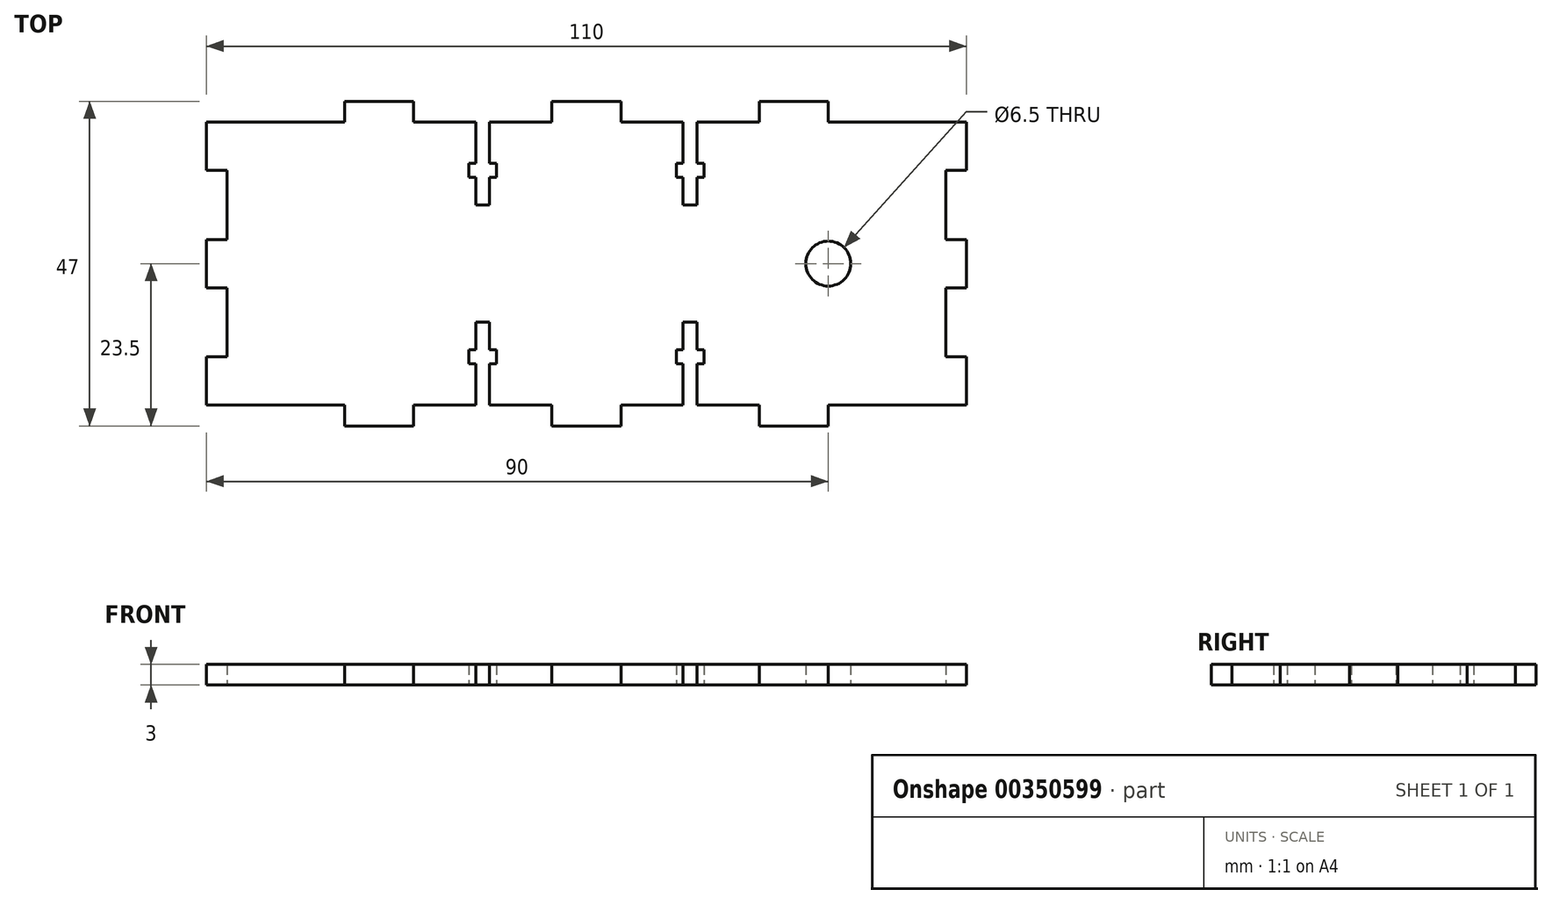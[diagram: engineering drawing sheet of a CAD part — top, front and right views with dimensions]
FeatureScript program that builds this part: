
annotation { "Feature Type Name" : "Feature", "Feature Type Description" : "" }
export const myFeature = defineFeature(function(context is Context, id is Id, definition is map)
    precondition{}
    {
        {
            var Q0;
            Q0=qCreatedBy(makeId("Top.planeOp"),FACE);
            var sketch = newSketch(context, id + "F0", { "sketchPlane" : qUnion([Q0])});
            skLineSegment(sketch, "E0", {"start": v(-110, 44) * mm, "end": v(-90, 44) * mm});
            skLineSegment(sketch, "E1", {"start": v(-90, 44) * mm, "end": v(-90, 47) * mm});
            skLineSegment(sketch, "E2", {"start": v(-90, 47) * mm, "end": v(-80, 47) * mm});
            skLineSegment(sketch, "E3", {"start": v(-80, 47) * mm, "end": v(-80, 44) * mm});
            skLineSegment(sketch, "E4", {"start": v(-60, 44) * mm, "end": v(-60, 47) * mm});
            skLineSegment(sketch, "E5", {"start": v(-60, 0) * mm, "end": v(-60, 3) * mm});
            skLineSegment(sketch, "E6", {"start": v(-80, 3) * mm, "end": v(-80, 0) * mm});
            skLineSegment(sketch, "E7", {"start": v(-80, 0) * mm, "end": v(-90, 0) * mm});
            skLineSegment(sketch, "E8", {"start": v(-90, 0) * mm, "end": v(-90, 3) * mm});
            skLineSegment(sketch, "E9", {"start": v(-90, 3) * mm, "end": v(-110, 3) * mm});
            skLineSegment(sketch, "E10", {"start": v(-110, 44) * mm, "end": v(-110, 37) * mm});
            skLineSegment(sketch, "E11", {"start": v(-110, 37) * mm, "end": v(-107, 37) * mm});
            skLineSegment(sketch, "E12", {"start": v(-107, 37) * mm, "end": v(-107, 27) * mm});
            skLineSegment(sketch, "E13", {"start": v(-107, 27) * mm, "end": v(-110, 27) * mm});
            skLineSegment(sketch, "E14", {"start": v(-110, 27) * mm, "end": v(-110, 20) * mm});
            skLineSegment(sketch, "E15", {"start": v(-110, 20) * mm, "end": v(-107, 20) * mm});
            skLineSegment(sketch, "E16", {"start": v(-107, 20) * mm, "end": v(-107, 10) * mm});
            skLineSegment(sketch, "E17", {"start": v(-107, 10) * mm, "end": v(-110, 10) * mm});
            skLineSegment(sketch, "E18", {"start": v(-110, 10) * mm, "end": v(-110, 3) * mm});
            skLineSegment(sketch, "E19", {"start": v(-80, 3) * mm, "end": v(-71, 3) * mm});
            skLineSegment(sketch, "E20", {"start": v(-71, 3) * mm, "end": v(-71, 9) * mm});
            skLineSegment(sketch, "E21", {"start": v(-71, 9) * mm, "end": v(-72, 9) * mm});
            skLineSegment(sketch, "E22", {"start": v(-72, 9) * mm, "end": v(-72, 11) * mm});
            skLineSegment(sketch, "E23", {"start": v(-72, 11) * mm, "end": v(-71, 11) * mm});
            skLineSegment(sketch, "E24", {"start": v(-71, 11) * mm, "end": v(-71, 15) * mm});
            skLineSegment(sketch, "E25", {"start": v(-71, 15) * mm, "end": v(-69, 15) * mm});
            skLineSegment(sketch, "E26", {"start": v(-69, 15) * mm, "end": v(-69, 11) * mm});
            skLineSegment(sketch, "E27", {"start": v(-69, 11) * mm, "end": v(-68, 11) * mm});
            skLineSegment(sketch, "E28", {"start": v(-68, 11) * mm, "end": v(-68, 9) * mm});
            skLineSegment(sketch, "E29", {"start": v(-68, 9) * mm, "end": v(-69, 9) * mm});
            skLineSegment(sketch, "E30", {"start": v(-69, 9) * mm, "end": v(-69, 3) * mm});
            skLineSegment(sketch, "E31", {"start": v(-80, 44) * mm, "end": v(-71, 44) * mm});
            skLineSegment(sketch, "E32", {"start": v(-60, 44) * mm, "end": v(-69, 44) * mm});
            skLineSegment(sketch, "E33", {"start": v(-69, 44) * mm, "end": v(-69, 38) * mm});
            skLineSegment(sketch, "E34", {"start": v(-69, 38) * mm, "end": v(-68, 38) * mm});
            skLineSegment(sketch, "E35", {"start": v(-68, 38) * mm, "end": v(-68, 36) * mm});
            skLineSegment(sketch, "E36", {"start": v(-68, 36) * mm, "end": v(-69, 36) * mm});
            skLineSegment(sketch, "E37", {"start": v(-69, 36) * mm, "end": v(-69, 32) * mm});
            skLineSegment(sketch, "E38", {"start": v(-69, 32) * mm, "end": v(-71, 32) * mm});
            skLineSegment(sketch, "E39", {"start": v(-71, 32) * mm, "end": v(-71, 36) * mm});
            skLineSegment(sketch, "E40", {"start": v(-71, 36) * mm, "end": v(-72, 36) * mm});
            skLineSegment(sketch, "E41", {"start": v(-72, 36) * mm, "end": v(-72, 38) * mm});
            skLineSegment(sketch, "E42", {"start": v(-72, 38) * mm, "end": v(-71, 38) * mm});
            skLineSegment(sketch, "E43", {"start": v(-71, 38) * mm, "end": v(-71, 44) * mm});
            skLineSegment(sketch, "E44", {"start": v(-69, 3) * mm, "end": v(-60, 3) * mm});
            skLineSegment(sketch, "E45", {"start": v(-60, 47) * mm, "end": v(-55, 47) * mm});
            skLineSegment(sketch, "E46", {"start": v(-60, 0) * mm, "end": v(-55, 0) * mm});
            skLineSegment(sketch, "E47.MirrorCS", {"start": v(-42, 38) * mm, "end": v(-42, 36) * mm});
            skLineSegment(sketch, "E48.MirrorCS", {"start": v(-41, 38) * mm, "end": v(-42, 38) * mm});
            skLineSegment(sketch, "E49.MirrorCS", {"start": v(-42, 9) * mm, "end": v(-41, 9) * mm});
            skLineSegment(sketch, "E50.MirrorCS", {"start": v(-42, 36) * mm, "end": v(-41, 36) * mm});
            skLineSegment(sketch, "E51.MirrorCS", {"start": v(-39, 32) * mm, "end": v(-39, 36) * mm});
            skLineSegment(sketch, "E52.MirrorCS", {"start": v(-41, 32) * mm, "end": v(-39, 32) * mm});
            skLineSegment(sketch, "E53.MirrorCS", {"start": v(-42, 11) * mm, "end": v(-42, 9) * mm});
            skLineSegment(sketch, "E54.MirrorCS", {"start": v(-39, 36) * mm, "end": v(-38, 36) * mm});
            skLineSegment(sketch, "E55.MirrorCS", {"start": v(-38, 9) * mm, "end": v(-38, 11) * mm});
            skLineSegment(sketch, "E56.MirrorCS", {"start": v(-39, 15) * mm, "end": v(-41, 15) * mm});
            skLineSegment(sketch, "E57.MirrorCS", {"start": v(-39, 9) * mm, "end": v(-38, 9) * mm});
            skLineSegment(sketch, "E58.MirrorCS", {"start": v(-38, 11) * mm, "end": v(-39, 11) * mm});
            skLineSegment(sketch, "E59.MirrorCS", {"start": v(0, 37) * mm, "end": v(-3, 37) * mm});
            skLineSegment(sketch, "E60.MirrorCS", {"start": v(-50, 0) * mm, "end": v(-50, 3) * mm});
            skLineSegment(sketch, "E61.MirrorCS", {"start": v(-30, 3) * mm, "end": v(-30, 0) * mm});
            skLineSegment(sketch, "E62.MirrorCS", {"start": v(-50, 44) * mm, "end": v(-50, 47) * mm});
            skLineSegment(sketch, "E63.MirrorCS", {"start": v(-38, 36) * mm, "end": v(-38, 38) * mm});
            skLineSegment(sketch, "E64.MirrorCS", {"start": v(-3, 10) * mm, "end": v(0, 10) * mm});
            skLineSegment(sketch, "E65.MirrorCS", {"start": v(-41, 11) * mm, "end": v(-42, 11) * mm});
            skLineSegment(sketch, "E66.MirrorCS", {"start": v(-41, 15) * mm, "end": v(-41, 11) * mm});
            skLineSegment(sketch, "E67.MirrorCS", {"start": v(-38, 38) * mm, "end": v(-39, 38) * mm});
            skLineSegment(sketch, "E68.MirrorCS", {"start": v(-20, 0) * mm, "end": v(-20, 3) * mm});
            skLineSegment(sketch, "E69.MirrorCS", {"start": v(-3, 27) * mm, "end": v(0, 27) * mm});
            skLineSegment(sketch, "E70.MirrorCS", {"start": v(-39, 11) * mm, "end": v(-39, 15) * mm});
            skLineSegment(sketch, "E71.MirrorCS", {"start": v(-41, 36) * mm, "end": v(-41, 32) * mm});
            skLineSegment(sketch, "E72.MirrorCS", {"start": v(-20, 44) * mm, "end": v(-20, 47) * mm});
            skLineSegment(sketch, "E73.MirrorCS", {"start": v(-30, 47) * mm, "end": v(-30, 44) * mm});
            skLineSegment(sketch, "E74.MirrorCS", {"start": v(0, 20) * mm, "end": v(-3, 20) * mm});
            skLineSegment(sketch, "E75.MirrorCS", {"start": v(-39, 3) * mm, "end": v(-39, 9) * mm});
            skLineSegment(sketch, "E76.MirrorCS", {"start": v(-41, 44) * mm, "end": v(-41, 38) * mm});
            skLineSegment(sketch, "E77.MirrorCS", {"start": v(0, 10) * mm, "end": v(0, 3) * mm});
            skLineSegment(sketch, "E78.MirrorCS", {"start": v(-20, 3) * mm, "end": v(0, 3) * mm});
            skLineSegment(sketch, "E79.MirrorCS", {"start": v(-3, 37) * mm, "end": v(-3, 27) * mm});
            skLineSegment(sketch, "E80.MirrorCS", {"start": v(-39, 38) * mm, "end": v(-39, 44) * mm});
            skLineSegment(sketch, "E81.MirrorCS", {"start": v(0, 27) * mm, "end": v(0, 20) * mm});
            skLineSegment(sketch, "E82.MirrorCS", {"start": v(0, 44) * mm, "end": v(-20, 44) * mm});
            skLineSegment(sketch, "E83.MirrorCS", {"start": v(-3, 20) * mm, "end": v(-3, 10) * mm});
            skLineSegment(sketch, "E84.MirrorCS", {"start": v(-50, 47) * mm, "end": v(-55, 47) * mm});
            skLineSegment(sketch, "E85.MirrorCS", {"start": v(0, 44) * mm, "end": v(0, 37) * mm});
            skLineSegment(sketch, "E86.MirrorCS", {"start": v(-50, 0) * mm, "end": v(-55, 0) * mm});
            skLineSegment(sketch, "E87.MirrorCS", {"start": v(-41, 9) * mm, "end": v(-41, 3) * mm});
            skLineSegment(sketch, "E88.MirrorCS", {"start": v(-41, 3) * mm, "end": v(-50, 3) * mm});
            skLineSegment(sketch, "E89.MirrorCS", {"start": v(-30, 3) * mm, "end": v(-39, 3) * mm});
            skLineSegment(sketch, "E90.MirrorCS", {"start": v(-20, 47) * mm, "end": v(-30, 47) * mm});
            skLineSegment(sketch, "E91.MirrorCS", {"start": v(-30, 0) * mm, "end": v(-20, 0) * mm});
            skLineSegment(sketch, "E92.MirrorCS", {"start": v(-30, 44) * mm, "end": v(-39, 44) * mm});
            skLineSegment(sketch, "E93.MirrorCS", {"start": v(-50, 44) * mm, "end": v(-41, 44) * mm});
            skCircle(sketch, "E94", {"center": v(-20, 23.5) * mm, "radius": 3.25 * mm});
            skSolve(sketch);
        }
        {
            var Q0;
            Q0=makeQuery(id+"F0.imprint","IMPRINT",FACE,{"disambiguationData":[TD([[makeQuery(id+"F0.imprint","IMPRINT",EDGE,{"derivedFrom":sQuery(id+"F0.wireOp",EDGE,"E0")}),-1.0]])]});
            extrude(context, id + "F1", {"entities" : qUnion([Q0]), "depth" : 3 * mm});
        }
    });
